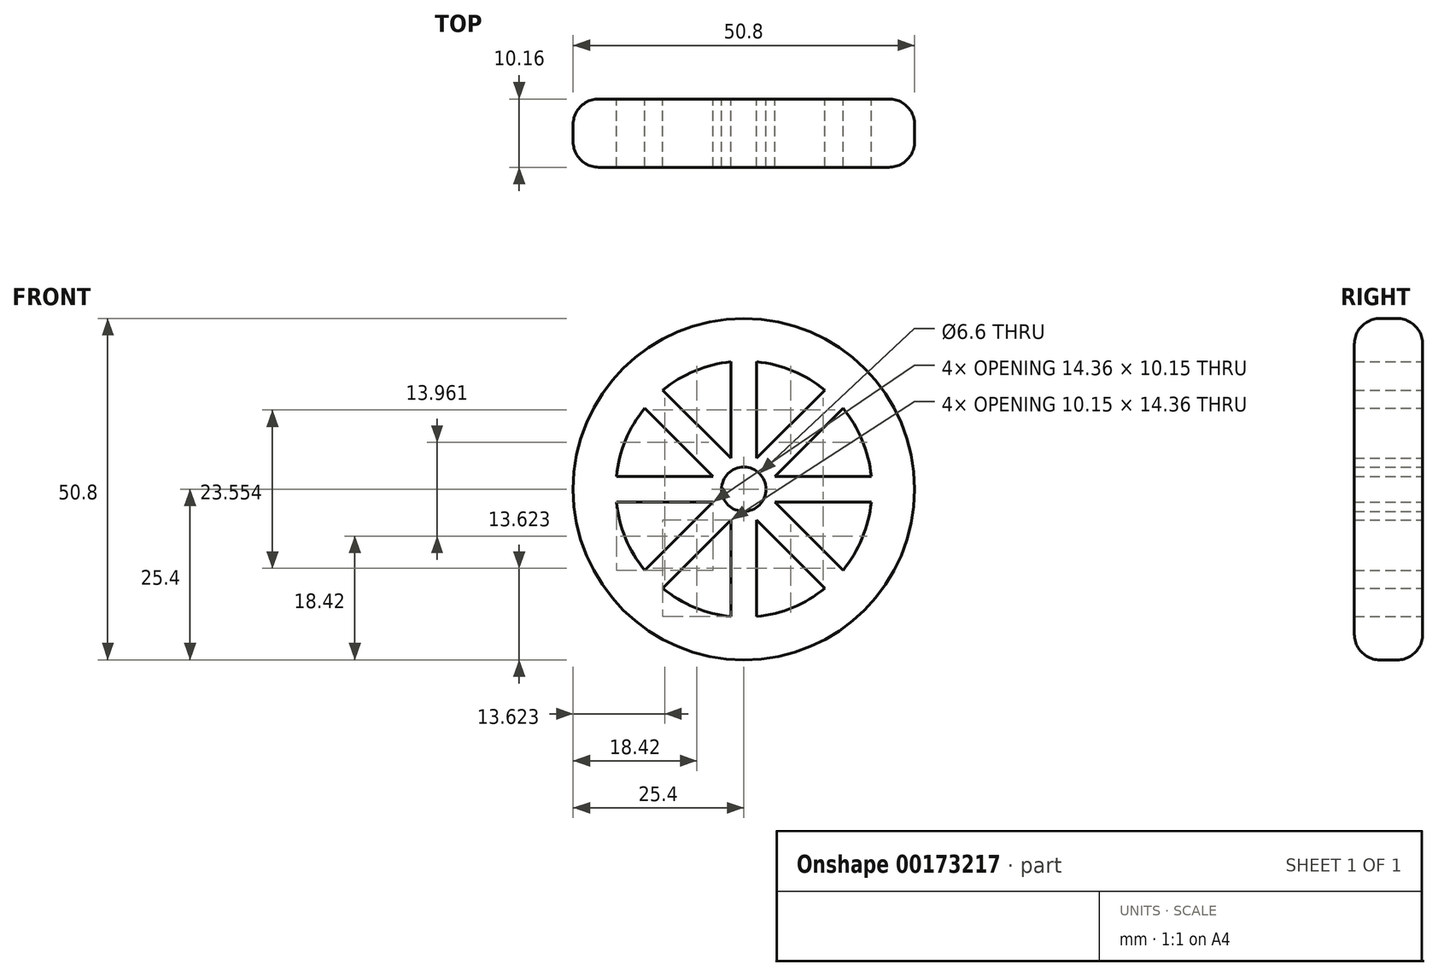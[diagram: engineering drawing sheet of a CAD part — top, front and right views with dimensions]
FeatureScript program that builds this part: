
annotation { "Feature Type Name" : "Feature", "Feature Type Description" : "" }
export const myFeature = defineFeature(function(context is Context, id is Id, definition is map)
    precondition{}
    {
        {
            var Q0;
            Q0=qCreatedBy(makeId("Front.planeOp"),FACE);
            var sketch = newSketch(context, id + "F0", { "sketchPlane" : qUnion([Q0])});
            skCircle(sketch, "E0", {"center": v(0, 0) * mm, "radius": 25.4 * mm});
            skCircle(sketch, "E1", {"center": v(0, 0) * mm, "radius": 19.05 * mm});
            skLineSegment(sketch, "E2.0", {"start": v(-14.82, 12.12) * mm, "end": v(-4.6, 1.9) * mm});
            skLineSegment(sketch, "E3.0", {"start": v(-12.12, 14.82) * mm, "end": v(-1.9, 4.6) * mm});
            skLineSegment(sketch, "E4.0", {"start": v(12.12, 14.82) * mm, "end": v(1.9, 4.6) * mm});
            skLineSegment(sketch, "E5.0", {"start": v(14.82, 12.12) * mm, "end": v(4.6, 1.9) * mm});
            skLineSegment(sketch, "E6.0", {"start": v(-19.05, -1.9) * mm, "end": v(-4.6, -1.9) * mm});
            skLineSegment(sketch, "E7.0", {"start": v(-19.05, 1.9) * mm, "end": v(-4.6, 1.9) * mm});
            skLineSegment(sketch, "E8.0", {"start": v(-1.9, 19.05) * mm, "end": v(-1.9, 4.6) * mm});
            skLineSegment(sketch, "E9.0", {"start": v(1.9, 19.05) * mm, "end": v(1.9, 4.6) * mm});
            skLineSegment(sketch, "E10.trimOffspring", {"start": v(-4.6, -1.9) * mm, "end": v(-14.82, -12.12) * mm});
            skLineSegment(sketch, "E11.trimOffspring", {"start": v(-1.9, -4.6) * mm, "end": v(-1.9, -19.05) * mm});
            skLineSegment(sketch, "E12.trimOffspring", {"start": v(4.6, 1.9) * mm, "end": v(19.05, 1.9) * mm});
            skLineSegment(sketch, "E13.trimOffspring", {"start": v(4.6, -1.9) * mm, "end": v(19.05, -1.9) * mm});
            skLineSegment(sketch, "E14.trimOffspring", {"start": v(4.6, -1.9) * mm, "end": v(14.82, -12.12) * mm});
            skLineSegment(sketch, "E15.trimOffspring", {"start": v(1.9, -4.6) * mm, "end": v(12.12, -14.82) * mm});
            skLineSegment(sketch, "E16.trimOffspring", {"start": v(-1.9, -4.6) * mm, "end": v(-12.12, -14.82) * mm});
            skPoint(sketch, "E17.orphan", {"position": v(-13.47, 13.47) * mm});
            skPoint(sketch, "E18.orphan", {"position": v(-19.05, 0) * mm});
            skPoint(sketch, "E19.trimOffspring.end.orphan", {"position": v(-13.47, -13.47) * mm});
            skLineSegment(sketch, "E20.trimOffspring", {"start": v(1.9, -4.6) * mm, "end": v(1.9, -19.05) * mm});
            skPoint(sketch, "E21.start.orphan", {"position": v(0, 19.05) * mm});
            skCircle(sketch, "E22", {"center": v(0, 0) * mm, "radius": 3.3 * mm});
            skSolve(sketch);
        }
        {
            var Q0;
            Q0=makeQuery(id+"F0.imprint","IMPRINT",FACE,{"disambiguationData":[TD([[makeQuery(id+"F0.imprint","IMPRINT",EDGE,{"derivedFrom":sQuery(id+"F0.wireOp",EDGE,"E0")}),1.0]])]});
            extrude(context, id + "F1", {"entities" : qUnion([Q0]), "endBound" : BoundingType.SYMMETRIC, "depth" : 10.16 * mm});
        }
        {
            var Q0;
            Q0=makeQuery(id+"F1.opExtrude","CAP_EDGE",EDGE,{"disambiguationData":[OSD([sQuery(id+"F0.wireOp",EDGE,"E0")])],"isStart":true});
            var Q1;
            Q1=makeQuery(id+"F1.opExtrude","CAP_EDGE",EDGE,{"disambiguationData":[OSD([sQuery(id+"F0.wireOp",EDGE,"E0")])],"isStart":false});
            fillet(context, id + "F2", {"entities" : qUnion([Q0, Q1]), "radius" : 3.8 * mm, "tangentPropagation" : true, "allowEdgeOverflow" : false});
        }
        {
            var Q0;
            {var subQ3=sQuery(id+"F0.wireOp",EDGE,"E1");var subQ30=sQuery(id+"F0.wireOp",EDGE,"E5.0");var subQ32=makeQuery(id+"F0.imprint","INTERSECT",VERTEX,{"derivedFrom":[subQ3,subQ30]});Q0=makeQuery(id+"F0.imprint","IMPRINT",FACE,{"disambiguationData":[TD([[makeQuery(id+"F0.imprint","IMPRINT",EDGE,{"disambiguationData":[TD([[subQ32,-1.0]])],"derivedFrom":subQ3}),1.0]])]});}
            extrude(context, id + "F3", {"entities" : qUnion([Q0]), "operationType" : NewBodyOperationType.ADD, "endBound" : BoundingType.SYMMETRIC, "depth" : 10.16 * mm});
        }
    });
